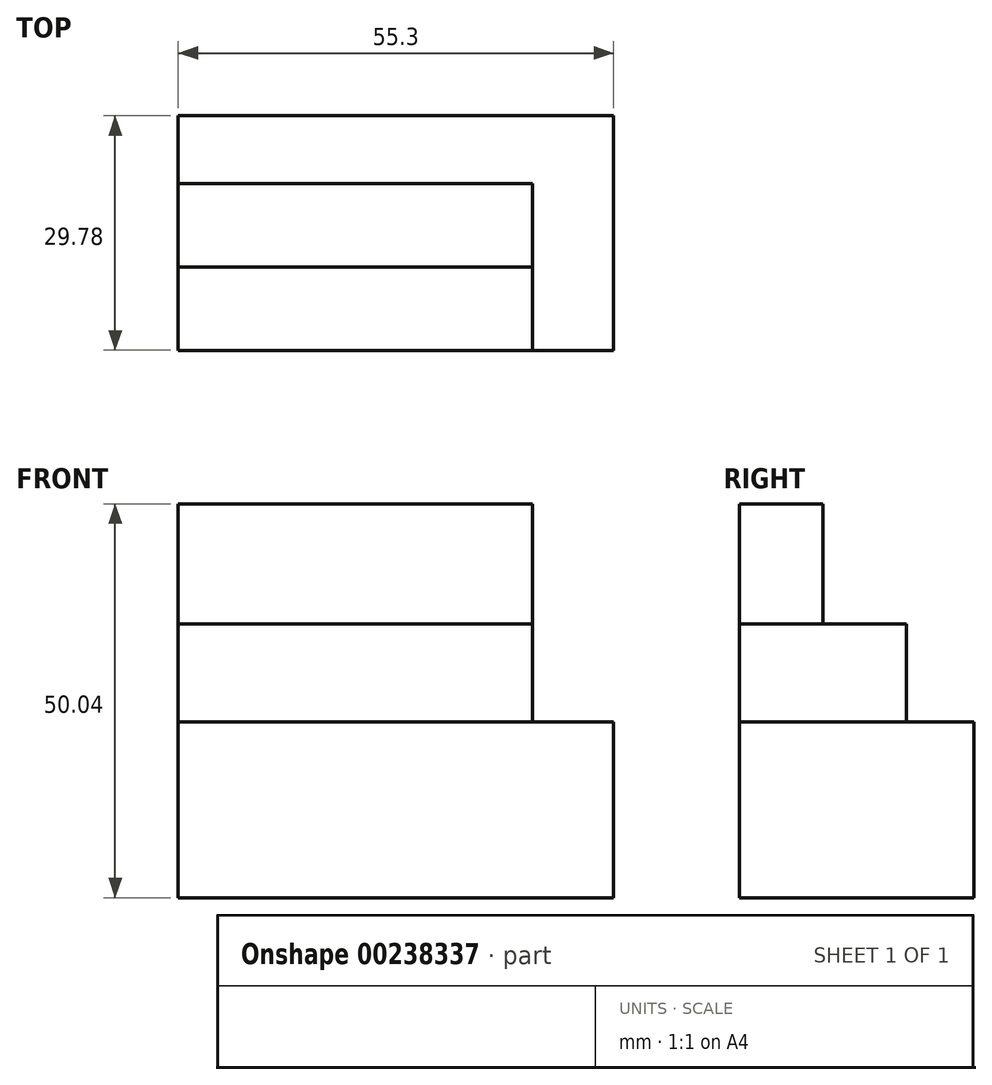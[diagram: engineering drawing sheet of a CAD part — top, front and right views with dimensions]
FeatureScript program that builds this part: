
annotation { "Feature Type Name" : "Feature", "Feature Type Description" : "" }
export const myFeature = defineFeature(function(context is Context, id is Id, definition is map)
    precondition{}
    {
        {
            var Q0;
            Q0=qCreatedBy(makeId("Top.planeOp"),FACE);
            var sketch = newSketch(context, id + "F0", { "sketchPlane" : qUnion([Q0])});
            skLineSegment(sketch, "E0.bottom", {"start": v(-27.65, -14.9) * mm, "end": v(27.65, -14.9) * mm});
            skLineSegment(sketch, "E0.top", {"start": v(-27.65, 14.9) * mm, "end": v(27.65, 14.9) * mm});
            skLineSegment(sketch, "E0.left", {"start": v(27.65, 14.9) * mm, "end": v(27.65, -14.9) * mm});
            skLineSegment(sketch, "E0.right", {"start": v(-27.65, 14.9) * mm, "end": v(-27.65, -14.9) * mm});
            skPoint(sketch, "E0.middle", {"position": v(0, 0) * mm});
            skSolve(sketch);
        }
        {
            var Q0;
            Q0 = qSketchRegion(id + "F0", true);
            extrude(context, id + "F1", {"entities" : qUnion([Q0]), "depth" : 22.35 * mm});
        }
        {
            var Q0;
            Q0=makeQuery(id+"F1.opExtrude","CAP_FACE",FACE,{"disambiguationData":[OSD([sQuery(id+"F0.wireOp",EDGE,"E0.bottom"),sQuery(id+"F0.wireOp",EDGE,"E0.top"),sQuery(id+"F0.wireOp",EDGE,"E0.left"),sQuery(id+"F0.wireOp",EDGE,"E0.right")])],"isStart":false});
            var sketch = newSketch(context, id + "F2", { "sketchPlane" : qUnion([Q0])});
            skLineSegment(sketch, "E1.bottom", {"start": v(-27.65, -14.9) * mm, "end": v(17.33, -14.9) * mm});
            skLineSegment(sketch, "E1.top", {"start": v(-27.65, 6.3) * mm, "end": v(17.33, 6.3) * mm});
            skLineSegment(sketch, "E1.left", {"start": v(-27.65, -14.9) * mm, "end": v(-27.65, 6.3) * mm});
            skLineSegment(sketch, "E1.right", {"start": v(17.33, -14.9) * mm, "end": v(17.33, 6.3) * mm});
            skSolve(sketch);
        }
        {
            var Q0;
            Q0 = qSketchRegion(id + "F2", true);
            extrude(context, id + "F3", {"entities" : qUnion([Q0]), "depth" : 12.45 * mm});
        }
        {
            var Q0;
            Q0=makeQuery(id+"F3.opExtrude","CAP_FACE",FACE,{"disambiguationData":[OSD([sQuery(id+"F2.wireOp",EDGE,"E1.bottom"),sQuery(id+"F2.wireOp",EDGE,"E1.top"),sQuery(id+"F2.wireOp",EDGE,"E1.left"),sQuery(id+"F2.wireOp",EDGE,"E1.right")])],"isStart":false});
            var sketch = newSketch(context, id + "F4", { "sketchPlane" : qUnion([Q0])});
            skLineSegment(sketch, "E2.bottom", {"start": v(-27.65, -14.9) * mm, "end": v(17.33, -14.9) * mm});
            skLineSegment(sketch, "E2.top", {"start": v(-27.65, -4.3) * mm, "end": v(17.33, -4.3) * mm});
            skLineSegment(sketch, "E2.left", {"start": v(-27.65, -14.9) * mm, "end": v(-27.65, -4.3) * mm});
            skLineSegment(sketch, "E2.right", {"start": v(17.33, -14.9) * mm, "end": v(17.33, -4.3) * mm});
            skSolve(sketch);
        }
        {
            var Q0;
            Q0 = qSketchRegion(id + "F4", true);
            extrude(context, id + "F5", {"entities" : qUnion([Q0]), "depth" : 15.24 * mm});
        }
    });
